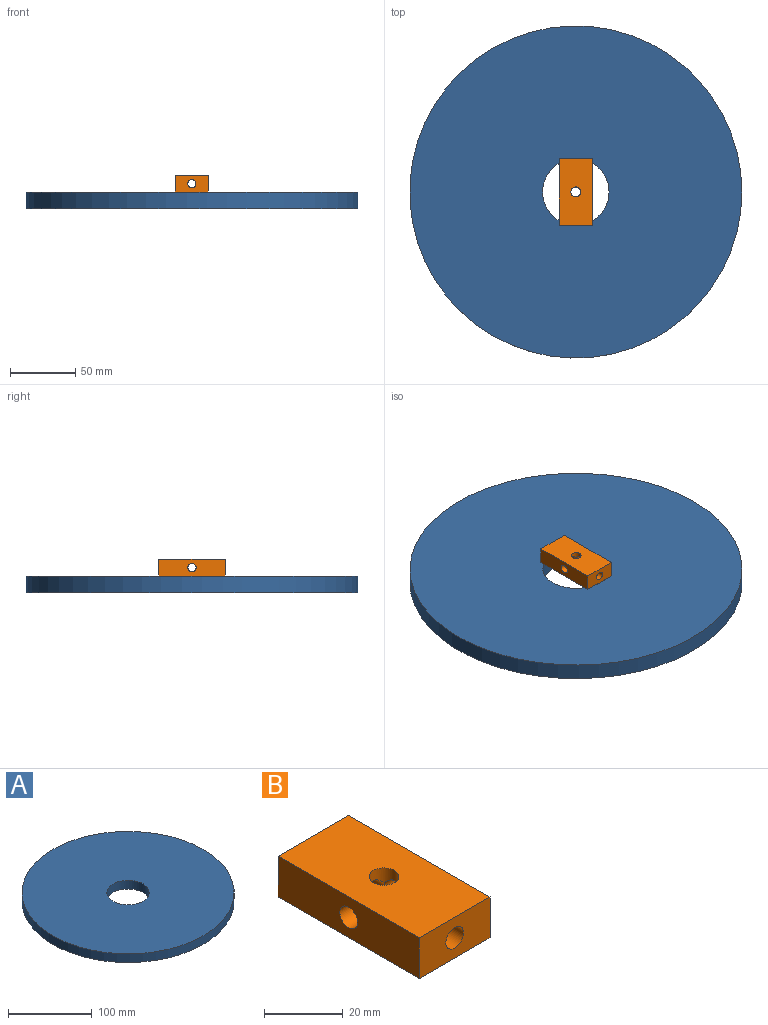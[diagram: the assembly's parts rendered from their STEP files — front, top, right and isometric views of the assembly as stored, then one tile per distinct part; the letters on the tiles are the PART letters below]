
ASSEMBLY  parts=2 mates=1
PART A: 4 faces, bbox 254x254x12.7 mm
  f0: cylinder r=127mm len=254mm, axis (0,0,-1), area 10134.1mm2, adj f1,f2
  f1: plane 254x254mm, normal (0,0,1), area 48643.9mm2, adj f0,f3
  f2: plane 254x254mm, normal (0,0,-1), area 48643.9mm2, adj f0,f3
  f3: cylinder r=25.4mm len=50.8mm, axis (0,0,1), area 2026.8mm2, adj f1,f2
PART B: 12 faces, bbox 25.4x50.8x12.7 mm
  f0: cylinder r=3.81mm len=7.62mm, axis (0,0,-1), area 87.5mm2, adj f7,f8,f9,f10,f11
  f1: plane 25.4x12.7mm, normal (0,-1,0), area 290.9mm2, adj f2,f4,f6,f7,f10
  f2: plane 50.8x12.7mm, normal (1,0,0), area 613.5mm2, adj f1,f3,f6,f7,f8
  f3: plane 25.4x12.7mm, normal (0,1,0), area 290.9mm2, adj f2,f4,f6,f7,f11
  f4: plane 50.8x12.7mm, normal (-1,0,0), area 613.5mm2, adj f1,f3,f6,f7,f9
  f5: cylinder r=3.81mm len=7.62mm, axis (0,0,-1), area 87.5mm2, adj f6,f8,f9,f10,f11
  f6: plane 50.8x25.4mm, normal (0,0,1), area 1244.7mm2, adj f1,f2,f3,f4,f5
  f7: plane 50.8x25.4mm, normal (0,0,-1), area 1244.7mm2, adj f0,f1,f2,f3,f4
  f8: cylinder r=3.17mm len=10.01mm, axis (1,0,0), area 188.2mm2, adj f0,f2,f5,f10,f11
  f9: cylinder r=3.17mm len=10.01mm, axis (1,0,0), area 188.2mm2, adj f0,f4,f5,f10,f11
  f10: cylinder r=3.17mm len=22.71mm, axis (0,1,0), area 441.6mm2, adj f0,f1,f5,f8,f9
  f11: cylinder r=3.17mm len=22.71mm, axis (0,1,0), area 441.6mm2, adj f0,f3,f5,f8,f9
PLACE A t=(-11.38,1.49,-19.71)mm
PLACE B t=(-24.08,26.89,-7.01)mm
MATE fastened A.f0 <-> B.f0  axis (0,0,1) through (-11.38,1.49,-7.01)mm
